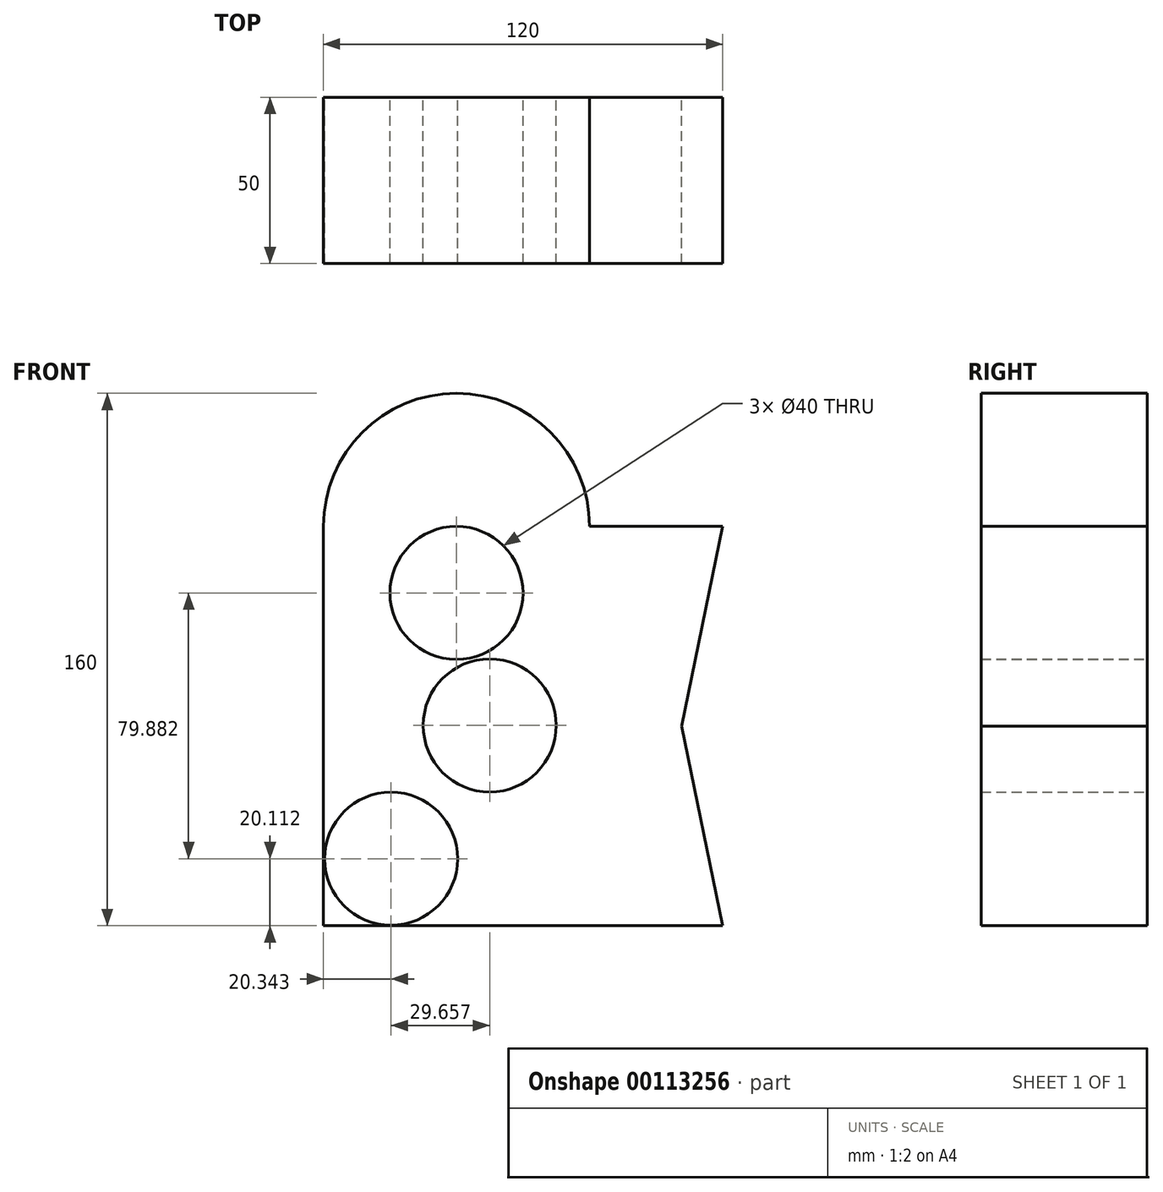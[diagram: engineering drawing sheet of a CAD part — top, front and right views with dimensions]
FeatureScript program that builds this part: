
annotation { "Feature Type Name" : "Feature", "Feature Type Description" : "" }
export const myFeature = defineFeature(function(context is Context, id is Id, definition is map)
    precondition{}
    {
        {
            var Q0;
            Q0=qCreatedBy(makeId("Front.planeOp"),FACE);
            var sketch = newSketch(context, id + "F0", { "sketchPlane" : qUnion([Q0])});
            skCircle(sketch, "E0", {"center": v(0, 58.4) * mm, "radius": 40 * mm});
            skLineSegment(sketch, "E1", {"start": v(-40, 58.4) * mm, "end": v(80, 58.4) * mm});
            skLineSegment(sketch, "E2", {"start": v(-40, 58.4) * mm, "end": v(-40, -61.6) * mm});
            skLineSegment(sketch, "E3", {"start": v(-40, -61.6) * mm, "end": v(80, -61.6) * mm});
            skLineSegment(sketch, "E4", {"start": v(80, 58.4) * mm, "end": v(67.66, -1.6) * mm});
            skLineSegment(sketch, "E5", {"start": v(67.66, -1.6) * mm, "end": v(80, -61.6) * mm});
            skLineSegment(sketch, "E6", {"start": v(40, 58.4) * mm, "end": v(40, -61.6) * mm});
            skCircle(sketch, "E7", {"center": v(0, 38.4) * mm, "radius": 20 * mm});
            skCircle(sketch, "E8", {"center": v(10, -1.43) * mm, "radius": 20 * mm});
            skCircle(sketch, "E9", {"center": v(-19.66, -41.49) * mm, "radius": 20 * mm});
            skSolve(sketch);
        }
        {
            var Q0;
            Q0 = qSketchRegion(id + "F0", true);
            extrude(context, id + "F1", {"entities" : qUnion([Q0]), "depth" : 50 * mm});
        }
    });
